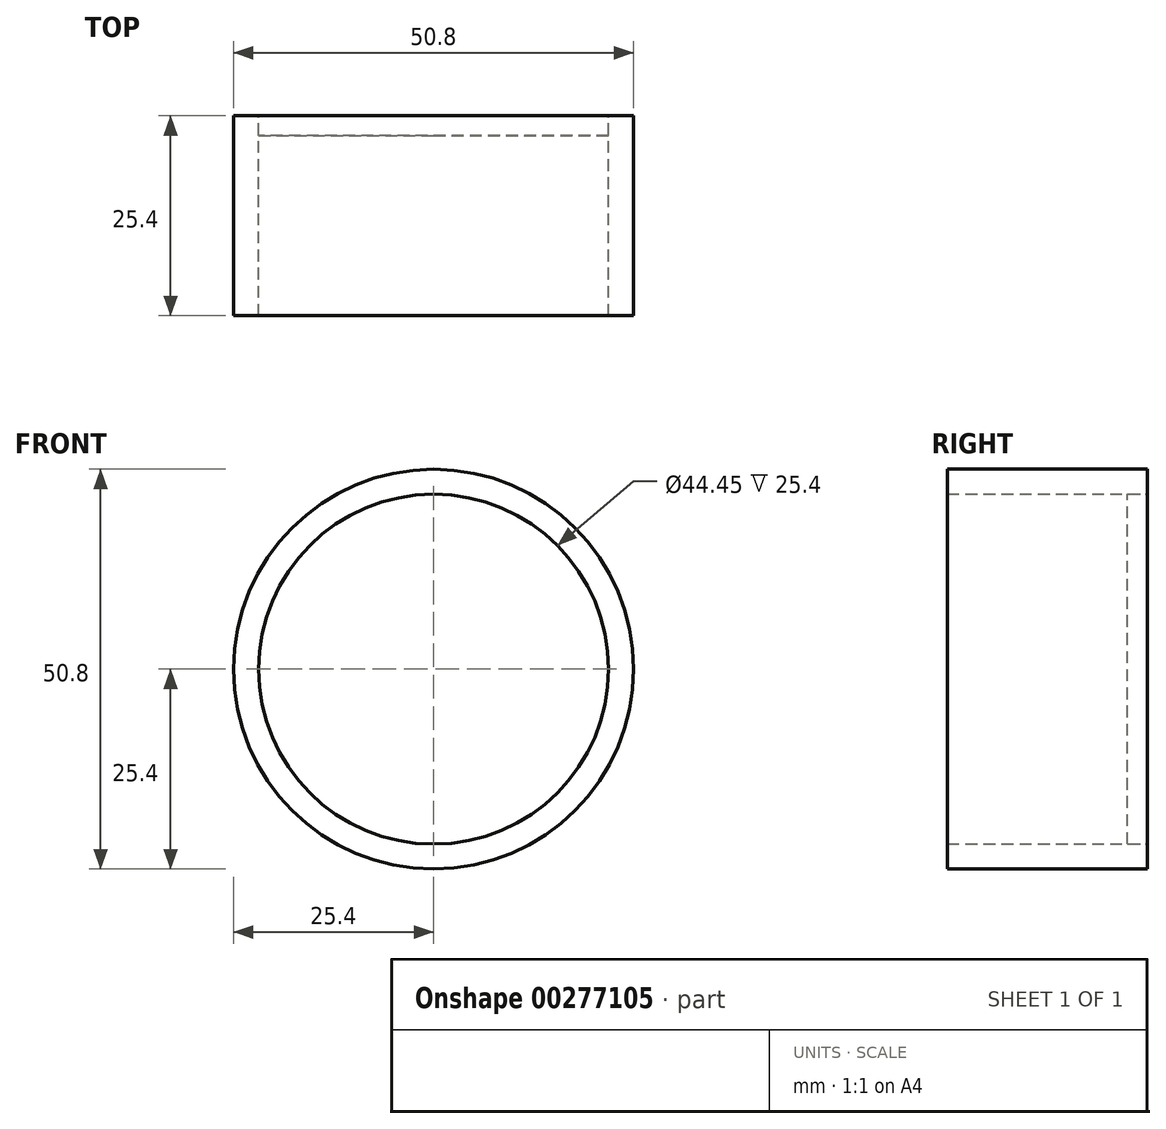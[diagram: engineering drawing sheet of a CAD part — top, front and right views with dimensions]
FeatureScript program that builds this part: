
annotation { "Feature Type Name" : "Feature", "Feature Type Description" : "" }
export const myFeature = defineFeature(function(context is Context, id is Id, definition is map)
    precondition{}
    {
        {
            var Q0;
            Q0=qCreatedBy(makeId("Front.planeOp"),FACE);
            var sketch = newSketch(context, id + "F0", { "sketchPlane" : qUnion([Q0])});
            skCircle(sketch, "E0", {"center": v(0, 0) * mm, "radius": 22.23 * mm});
            skCircle(sketch, "E1", {"center": v(0, 0) * mm, "radius": 25.4 * mm});
            skSolve(sketch);
        }
        {
            var Q0;
            Q0 = qSketchRegion(id + "F0", true);
            extrude(context, id + "F1", {"entities" : qUnion([Q0]), "depth" : 25.4 * mm});
        }
        {
            var Q0;
            Q0=makeQuery(id+"F0.imprint","IMPRINT",FACE,{"disambiguationData":[TD([[makeQuery(id+"F0.imprint","IMPRINT",EDGE,{"derivedFrom":sQuery(id+"F0.wireOp",EDGE,"E0")}),1.0]])]});
            extrude(context, id + "F2", {"entities" : qUnion([Q0]), "depth" : 2.54 * mm});
        }
    });
